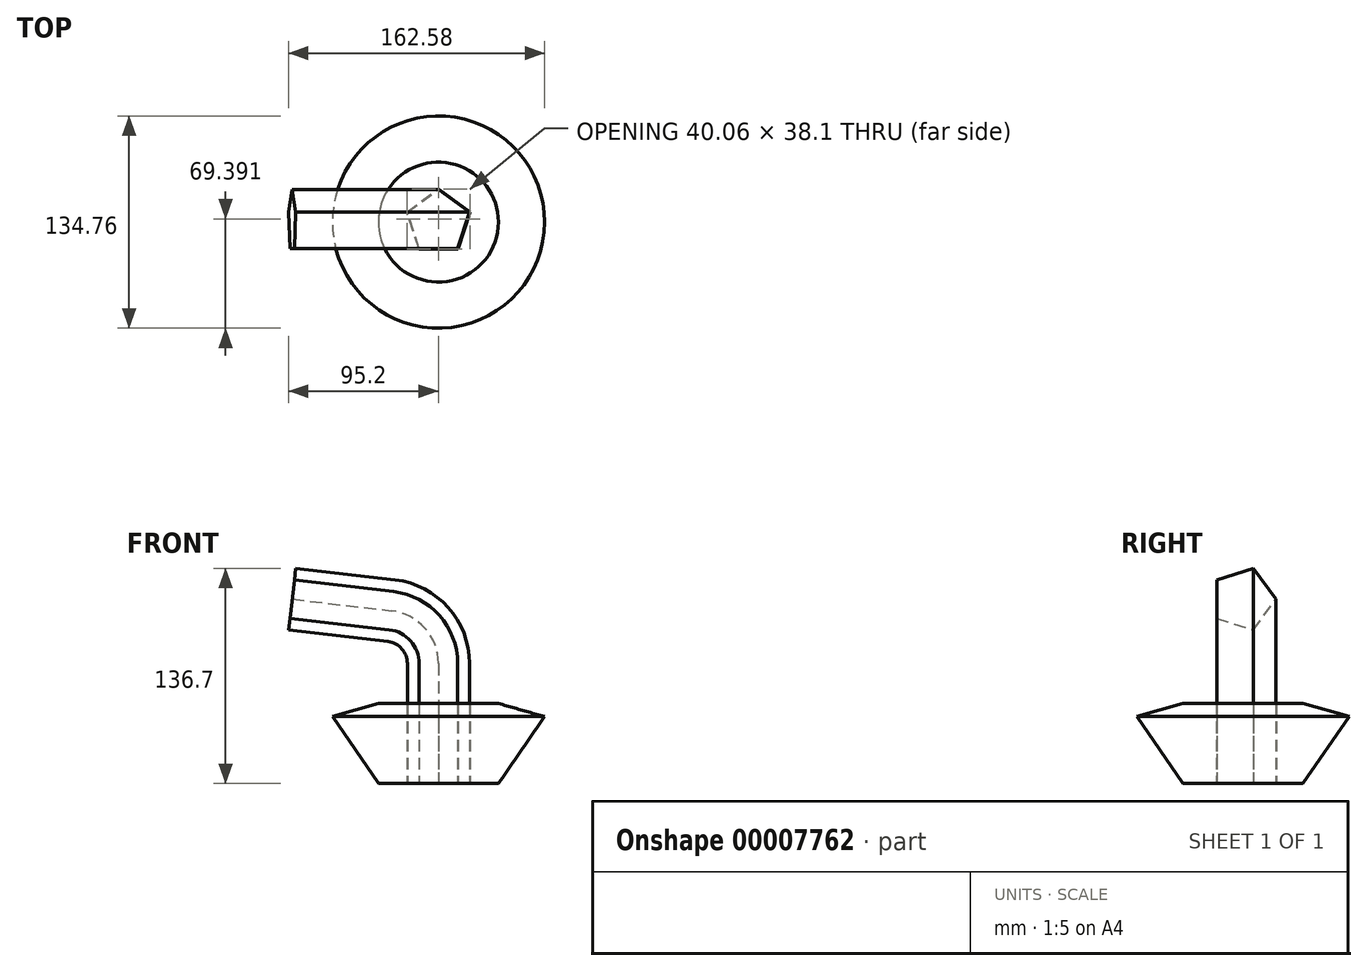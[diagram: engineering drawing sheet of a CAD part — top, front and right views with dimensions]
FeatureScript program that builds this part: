
annotation { "Feature Type Name" : "Feature", "Feature Type Description" : "" }
export const myFeature = defineFeature(function(context is Context, id is Id, definition is map)
    precondition{}
    {
        {
            var Q0;
            Q0=qCreatedBy(makeId("Top.planeOp"),FACE);
            var sketch = newSketch(context, id + "F0", { "sketchPlane" : qUnion([Q0])});
            skCircle(sketch, "E0", {"center": v(0, 0) * mm, "radius": 38.1 * mm});
            skCircle(sketch, "E1.cCircle", {"center": v(0, 0) * mm, "radius": 17.04 * mm, "construction": true});
            skLineSegment(sketch, "E1.0", {"start": v(20.03, 6.5) * mm, "end": v(12.38, -17.04) * mm});
            skLineSegment(sketch, "E1.1", {"start": v(12.38, -17.04) * mm, "end": v(-12.38, -17.04) * mm});
            skLineSegment(sketch, "E1.2", {"start": v(-12.38, -17.04) * mm, "end": v(-20.03, 6.5) * mm});
            skLineSegment(sketch, "E1.3", {"start": v(-20.03, 6.5) * mm, "end": v(0, 21.06) * mm});
            skLineSegment(sketch, "E1.4", {"start": v(0, 21.06) * mm, "end": v(20.03, 6.5) * mm});
            skPoint(sketch, "E1.0.midPoint", {"position": v(16.2, -5.27) * mm});
            skSolve(sketch);
        }
        {
            var Q0;
            Q0 = qSketchRegion(id + "F0", true);
            extrude(context, id + "F1", {"entities" : qUnion([Q0]), "depth" : 50.8 * mm});
        }
        {
            var Q0;
            Q0=qCreatedBy(makeId("Front.planeOp"),FACE);
            var sketch = newSketch(context, id + "F2", { "sketchPlane" : qUnion([Q0])});
            skLineSegment(sketch, "E2", {"start": v(-38.1, 50.8) * mm, "end": v(-67.38, 42.49) * mm});
            skLineSegment(sketch, "E3", {"start": v(-67.38, 42.49) * mm, "end": v(-38.1, 0) * mm});
            skLineSegment(sketch, "E4", {"start": v(-38.1, 0) * mm, "end": v(-38.1, 50.8) * mm});
            skLineSegment(sketch, "E5", {"start": v(0, 0) * mm, "end": v(0, 54.72) * mm, "construction": true});
            skSolve(sketch);
        }
        {
            var Q0;
            Q0 = qSketchRegion(id + "F2", true);
            var Q1;
            Q1=makeQuery(id+"F1.opExtrude","SWEPT_FACE",FACE,{"disambiguationData":[OSD([sQuery(id+"F0.wireOp",EDGE,"E0")])]});
            revolve(context, id + "F3", {"operationType" : NewBodyOperationType.ADD, "entities" : qUnion([Q0]), "axis" : qUnion([Q1]), "revolveType" : RevolveType.FULL});
        }
        {
            var Q0;
            Q0=qCreatedBy(makeId("Top.planeOp"),FACE);
            var sketch = newSketch(context, id + "F4", { "sketchPlane" : qUnion([Q0])});
            skLineSegment(sketch, "E6.0", {"start": v(-12.2, -16.78) * mm, "end": v(-19.73, 6.41) * mm});
            skLineSegment(sketch, "E6.1", {"start": v(12.2, -16.78) * mm, "end": v(-12.2, -16.78) * mm});
            skLineSegment(sketch, "E6.2", {"start": v(19.73, 6.41) * mm, "end": v(12.2, -16.78) * mm});
            skLineSegment(sketch, "E6.3", {"start": v(0, 20.75) * mm, "end": v(19.73, 6.41) * mm});
            skLineSegment(sketch, "E6.4", {"start": v(-19.73, 6.41) * mm, "end": v(0, 20.75) * mm});
            skSolve(sketch);
        }
        {
            var Q0;
            Q0 = qSketchRegion(id + "F4", true);
            extrude(context, id + "F5", {"entities" : qUnion([Q0]), "depth" : 54.56 * mm});
        }
        {
            var Q0;
            Q0=qCreatedBy(makeId("Front.planeOp"),FACE);
            var sketch = newSketch(context, id + "F6", { "sketchPlane" : qUnion([Q0])});
            skLineSegment(sketch, "E7", {"start": v(0, 54.56) * mm, "end": v(0, 76.19) * mm});
            skArc(sketch, "E8", {"start": v(0, 76.19) * mm, "mid": v(-8.54, 98.63) * mm, "end": v(-29.84, 109.72) * mm});
            skSolve(sketch);
        }
        {
            var Q0;
            Q0=makeQuery(id+"F5.opExtrude","CAP_FACE",FACE,{"disambiguationData":[OSD([sQuery(id+"F4.wireOp",EDGE,"E6.0"),sQuery(id+"F4.wireOp",EDGE,"E6.1"),sQuery(id+"F4.wireOp",EDGE,"E6.2"),sQuery(id+"F4.wireOp",EDGE,"E6.3"),sQuery(id+"F4.wireOp",EDGE,"E6.4")])],"isStart":false});
            var Q1;
            Q1=sQuery(id+"F6.wireOp",EDGE,"E7");
            var Q2;
            Q2=sQuery(id+"F6.wireOp",EDGE,"E8");
            sweep(context, id + "F7", {"operationType" : NewBodyOperationType.ADD, "profiles" : qUnion([Q0]), "path" : qUnion([Q1, Q2])});
        }
        {
            var Q0;
            Q0=makeQuery(id+"F7.opSweep","CAP_FACE",FACE,{"disambiguationData":[OSD([sQuery(id+"F4.wireOp",EDGE,"E6.0"),sQuery(id+"F4.wireOp",EDGE,"E6.1"),sQuery(id+"F4.wireOp",EDGE,"E6.2"),sQuery(id+"F4.wireOp",EDGE,"E6.3"),sQuery(id+"F4.wireOp",EDGE,"E6.4"),sQuery(id+"F6.wireOp",VERTEX,"E8.end")])],"isStart":false});
            extrude(context, id + "F8", {"entities" : qUnion([Q0]), "operationType" : NewBodyOperationType.ADD, "depth" : 63.5 * mm});
        }
    });
